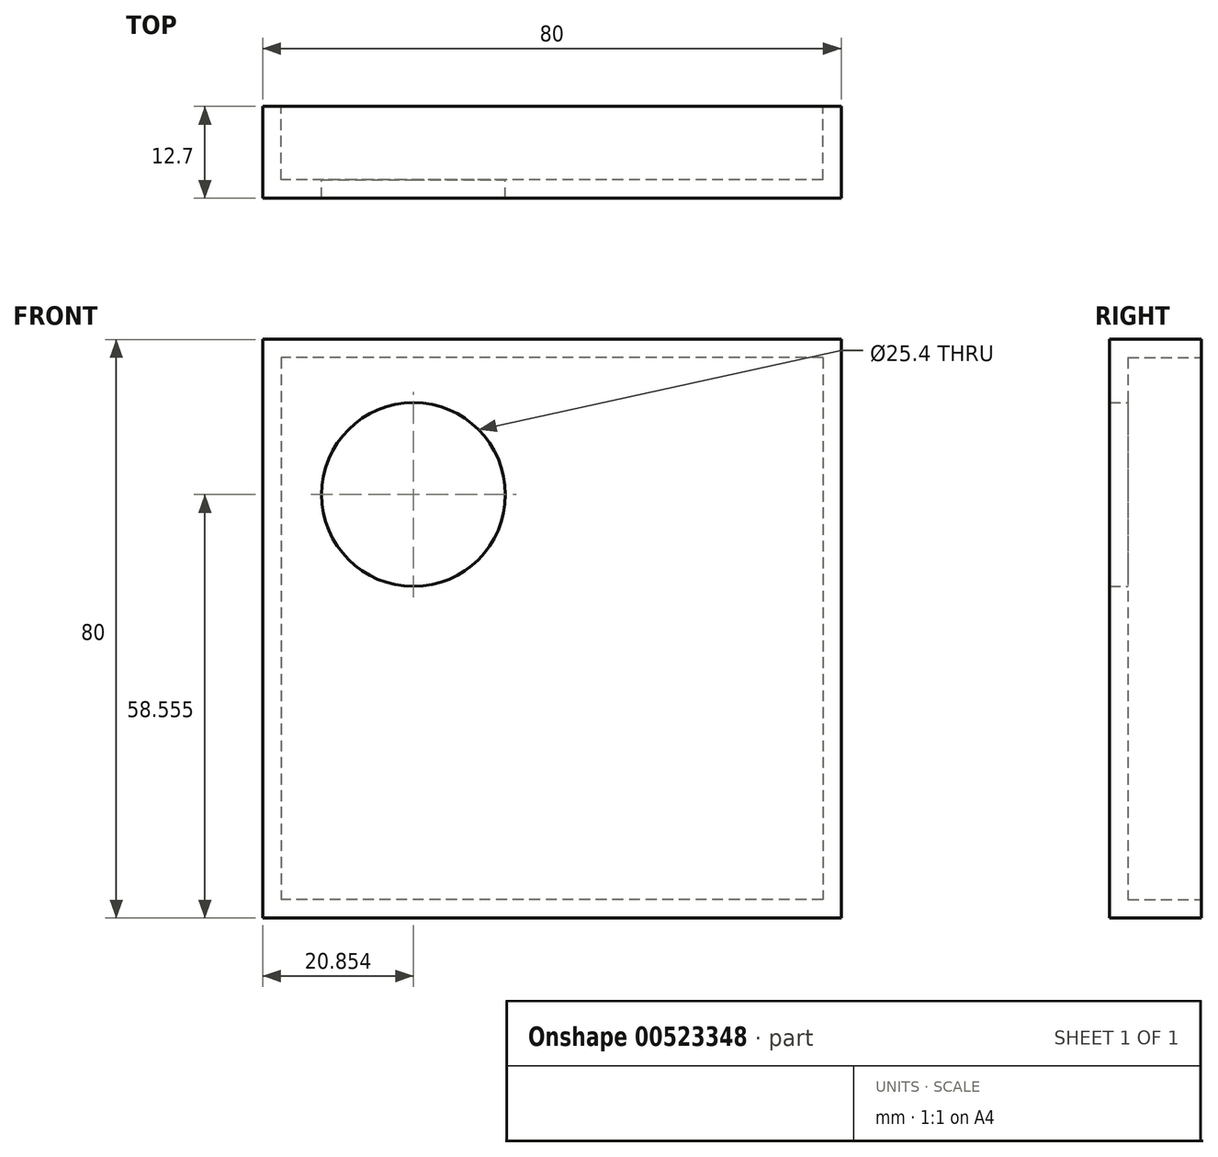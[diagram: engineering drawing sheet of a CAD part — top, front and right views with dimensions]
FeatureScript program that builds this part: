
annotation { "Feature Type Name" : "Feature", "Feature Type Description" : "" }
export const myFeature = defineFeature(function(context is Context, id is Id, definition is map)
    precondition{}
    {
        {
            var Q0;
            Q0=qCreatedBy(makeId("Front.planeOp"),FACE);
            var sketch = newSketch(context, id + "F0", { "sketchPlane" : qUnion([Q0])});
            skLineSegment(sketch, "E0.bottom", {"start": v(-40, 40) * mm, "end": v(40, 40) * mm});
            skLineSegment(sketch, "E0.top", {"start": v(-40, -40) * mm, "end": v(40, -40) * mm});
            skLineSegment(sketch, "E0.left", {"start": v(-40, 40) * mm, "end": v(-40, -40) * mm});
            skLineSegment(sketch, "E0.right", {"start": v(40, 40) * mm, "end": v(40, -40) * mm});
            skPoint(sketch, "E0.middle", {"position": v(0, 0) * mm});
            skSolve(sketch);
        }
        {
            var Q0;
            Q0=qSketchRegion(id+"F0",true);
            extrude(context, id + "F1", {"entities" : qUnion([Q0]), "depth" : 12.7 * mm, "offsetDistance" : 25.4 * mm});
        }
        {
            var Q0;
            Q0=makeQuery(id+"F1.opExtrude","CAP_FACE",FACE,{"disambiguationData":[OSD([sQuery(id+"F0.wireOp",EDGE,"E0.bottom"),sQuery(id+"F0.wireOp",EDGE,"E0.top"),sQuery(id+"F0.wireOp",EDGE,"E0.left"),sQuery(id+"F0.wireOp",EDGE,"E0.right")])],"isStart":true});
            var sketch = newSketch(context, id + "F2", { "sketchPlane" : qUnion([Q0])});
            skLineSegment(sketch, "E1.bottom", {"start": v(-37.47, 37.47) * mm, "end": v(37.47, 37.47) * mm});
            skLineSegment(sketch, "E1.top", {"start": v(-37.47, -37.47) * mm, "end": v(37.47, -37.47) * mm});
            skLineSegment(sketch, "E1.left", {"start": v(-37.47, 37.47) * mm, "end": v(-37.47, -37.47) * mm});
            skLineSegment(sketch, "E1.right", {"start": v(37.47, 37.47) * mm, "end": v(37.47, -37.47) * mm});
            skPoint(sketch, "E1.middle", {"position": v(0, 0) * mm});
            skSolve(sketch);
        }
        {
            var Q0;
            Q0=qSketchRegion(id+"F2",true);
            extrude(context, id + "F3", {"entities" : qUnion([Q0]), "operationType" : NewBodyOperationType.REMOVE, "oppositeDirection" : true, "depth" : 10.16 * mm, "offsetDistance" : 25.4 * mm});
        }
        {
            var Q0;
            Q0=makeQuery(id+"F3.boolean.opBoolean","COPY",FACE,{"derivedFrom":makeQuery(id+"F3.opExtrude","CAP_FACE",FACE,{"disambiguationData":[OSD([sQuery(id+"F2.wireOp",EDGE,"E1.bottom"),sQuery(id+"F2.wireOp",EDGE,"E1.top"),sQuery(id+"F2.wireOp",EDGE,"E1.left"),sQuery(id+"F2.wireOp",EDGE,"E1.right")])],"isStart":false})});
            var sketch = newSketch(context, id + "F4", { "sketchPlane" : qUnion([Q0])});
            skCircle(sketch, "E2", {"center": v(19.15, 18.55) * mm, "radius": 12.7 * mm});
            skSolve(sketch);
        }
        {
            var Q0;
            Q0=makeQuery(id+"F4.imprint","IMPRINT",FACE,{"disambiguationData":[TD([[makeQuery(id+"F4.imprint","IMPRINT",EDGE,{"derivedFrom":sQuery(id+"F4.wireOp",EDGE,"E2")}),1.0]])]});
            extrude(context, id + "F5", {"entities" : qUnion([Q0]), "operationType" : NewBodyOperationType.REMOVE, "oppositeDirection" : true, "depth" : 25.4 * mm, "offsetDistance" : 25.4 * mm});
        }
    });
